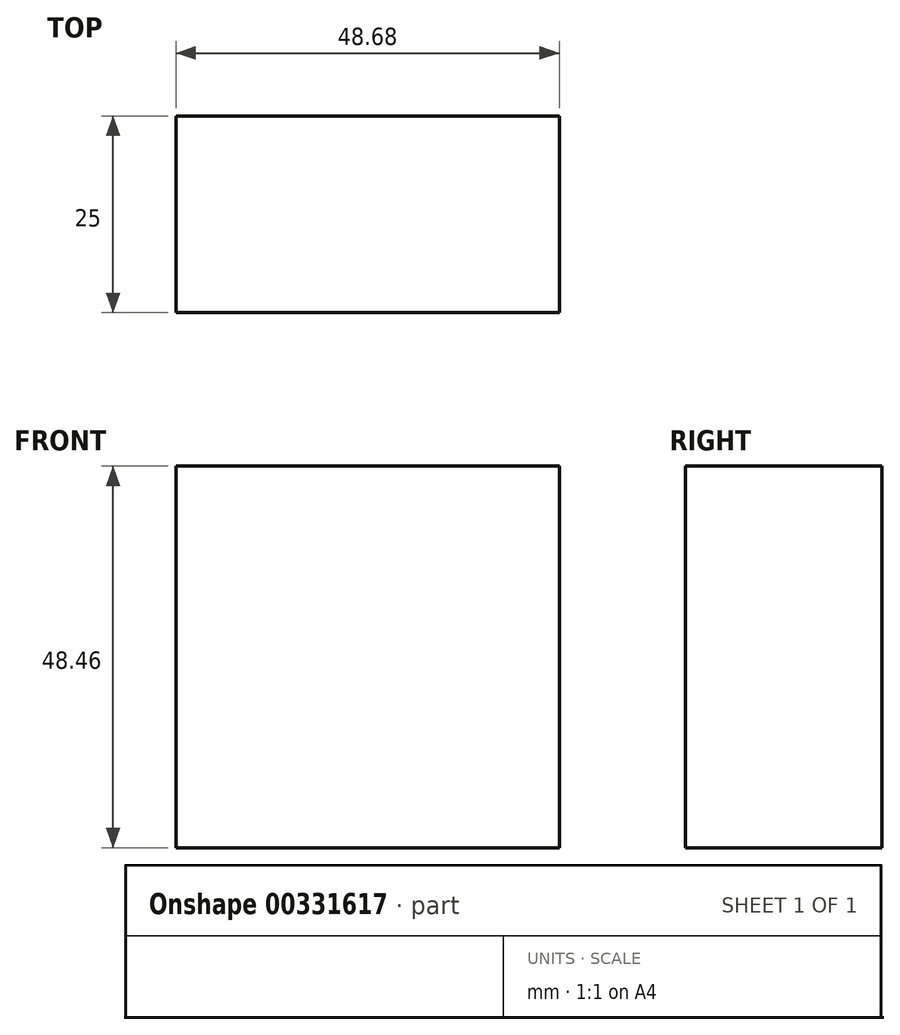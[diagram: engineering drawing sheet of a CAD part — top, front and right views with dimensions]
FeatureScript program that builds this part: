
annotation { "Feature Type Name" : "Feature", "Feature Type Description" : "" }
export const myFeature = defineFeature(function(context is Context, id is Id, definition is map)
    precondition{}
    {
        {
            var Q0;
            Q0=qCreatedBy(makeId("Front.planeOp"),FACE);
            var sketch = newSketch(context, id + "F0", { "sketchPlane" : qUnion([Q0])});
            skLineSegment(sketch, "E0.bottom", {"start": v(-85.03, 11.48) * mm, "end": v(-36.35, 11.48) * mm});
            skLineSegment(sketch, "E0.top", {"start": v(-85.03, 59.94) * mm, "end": v(-36.35, 59.94) * mm});
            skLineSegment(sketch, "E0.left", {"start": v(-85.03, 11.48) * mm, "end": v(-85.03, 59.94) * mm});
            skLineSegment(sketch, "E0.right", {"start": v(-36.35, 11.48) * mm, "end": v(-36.35, 59.94) * mm});
            skPoint(sketch, "E0.middle", {"position": v(-60.7, 35.7) * mm});
            skSolve(sketch);
        }
        {
            var Q0;
            Q0=makeQuery(id+"F0.imprint","IMPRINT",FACE,{"disambiguationData":[TD([[makeQuery(id+"F0.imprint","IMPRINT",EDGE,{"derivedFrom":sQuery(id+"F0.wireOp",EDGE,"E0.bottom")}),1.0]])]});
            extrude(context, id + "F1", {"entities" : qUnion([Q0]), "depth" : 25 * mm});
        }
    });
